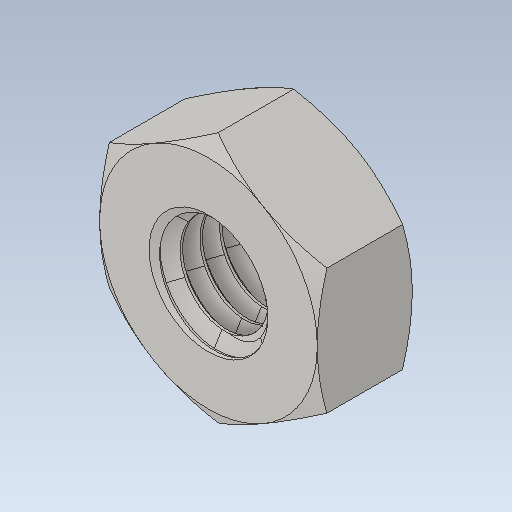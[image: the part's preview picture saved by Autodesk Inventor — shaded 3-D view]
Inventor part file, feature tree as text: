
AUTODESK INVENTOR PART (.ipt)
format: ipt  version: 2020.2 (Build 242310000, 310)  size: 442,368 bytes
history: imported  units: mm
features: imported_body x1
ambient origin geometry x8: Origin, YZ Plane, XZ Plane, XY Plane, X Axis, Y Axis, Z Axis, Center Point
bodies: Solide1 (imported_parasolid), Body1 (imported_parasolid)
feature tree (1):
  imported_body  NMx_Import_Brep_tag  [imported B-rep: ~3 faces, bbox_mm=None]
